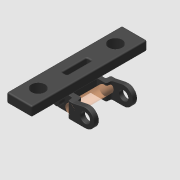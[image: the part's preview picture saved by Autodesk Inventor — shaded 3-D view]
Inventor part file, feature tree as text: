
AUTODESK INVENTOR PART (.ipt)
format: ipt  version: 2021 (Build 250183000, 183)  size: 703,488 bytes
history: native  units: in
note: dims shown in document units (in); Inventor stores cm internally (conversion verified against a paired STEP export)
features: other x4, extrude x3, sketch x2, imported_body x1
ambient origin geometry x8: Origin, YZ Plane, XZ Plane, XY Plane, X Axis, Y Axis, Z Axis, Center Point
bodies: Body1 (feature_tree), Body2 (feature_tree), Body3 (feature_tree), Body4 (feature_tree)
feature tree (10):
  parser-record x1  (decoder bookkeeping rows leaked as tree rows — omitted from the tree; the rows remain in map.json)
  imported_body  "Base1"
  other  "Srf1"
  sketch  "Sketch2"  dims[d11=0.0in d12=0.0in]
  other  "Srf2"
  sketch  "Sketch4"  dims[d13=0.0in d14=0.0in d18=0.063in d19=0.0in d20=0.0in d22=0.063in d23=0.0in d24=0.0in d25=0.0in d26=0.0in d27=0.125in d30=1.0in d31=0.0in]
  other  "Srf3"
  extrude  "ExtrusionSrf1"  TaperAngle=0.0deg  [1 undecoded]
  extrude  "ExtrusionSrf2"  TaperAngle=0.0deg  [1 undecoded]
  extrude  "ExtrusionSrf3"  Depth=0.063in TaperAngle=0.0deg
note: 2 required parameter values undecoded (feature->parameter linkage not recoverable at this tier; creation-order binding heuristic only, values carry confidence <= 0.55)
